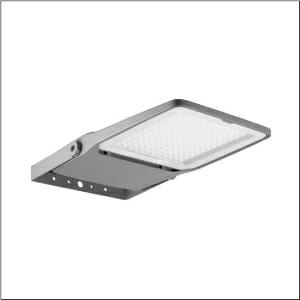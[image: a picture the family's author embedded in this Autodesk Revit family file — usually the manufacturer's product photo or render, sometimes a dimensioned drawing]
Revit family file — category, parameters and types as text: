
# Revit family: floodlight_fl_20_midi___rs17_5xa7682e3b2ac_f562
name_source: partatom
category: Lighting Fixtures
units: mm (PartAtom-declared; Revit-internal decimal feet)

## family parameters
Cut with Voids When Loaded = No
Host = Face
Light Source = No
Part Type = Normal
Room Calculation Point = No
Round Connector Dimension = Use Diameter
Shared = No

## types (1)
- --- (1 x LED 5000K / CRI = 70 (unbekannt), 29600 lm, 5000K)
    Apparent Load = 208 VA
    CIE Flux Codes = 79 92 99 100 100
    Color Rendering = 70
    Color Temperature = 5000K
    Default Elevation = 1800 mm
    Description = Floodlight FL 20 midi, floodlight, primary light control with lens, of plastic, primary optical cover: protective disc, of toughened safety glass, transparent, light distribution: RS17, light emission: direct distribution, primary light characteristic: rotationally symmetric, installation type: surface-mounted, LED, High Power LED, rated luminous flux: 29.600lm, luminous efficacy: 142lm/W, light colour: 750, colour temperature: 5000K, control gear: ECG Plus, control: flexible luminous flux parameterisation, time-dependent luminous flux control, digital communication interface, power reduction, overheat protection, electronic power reduction, with terminal, 5-pole, max. 2.5mm², mains connection: 220..240V, AC, 50/60Hz, rated input power: 208W, LED unit, of diecast aluminium, powder-coated, Siteco® metallic grey (DB 702S), corrosivity category C5 mid according to DIN EN ISO 12944, incl. 1x M20 cable gland for cable Ø 6.5..12mm, length: 731mm, width: 450mm, height: 76mm, housing frame, of diecast aluminium, powder-coated, Siteco® metallic grey (DB 702S), wall fastening, of steel, powder-coated, Siteco® metallic grey (DB 702S), DALI, protection rating (complete): IP66, insulation class (complete): insulation class II (safety insulation), certification: CE, ENEC, VDE, protection symbol: D, permissible operating ambient temperature: -40..+40°C, permissible operating ambient temperature for outdoor applications: -40..+50°C, standard: DIN EN 12944, packaging unit: 1 piece

Light Distribution: RS17
    Height = 76 mm
    Lamp = 1 x LED 5000K / CRI >= 70 (unbekannt)
    Lamp Light Flux = 29600 lm
    Lamp count = 1
    Length = 731 mm
    Luminous efficacy = 142 lm/W
    Manufacturer = Siteco
    ModVariant = No
    Model = 5XA7682E3B2AC
    Mounting Place = Wall
    Mounting Type = Surface mounted
    Number of Poles = 1
    OnlyDefault = Yes
    Power Factor = 1
    Product Name = Floodlight FL 20 midi | RS17
    Product group = floodlight | wall mounted
    ProductGroupID = 2001
    Protection Class = Protection class II
    Protection Degree = IP 66
    RLX_Detail_Level = 1
    RLX_Emergency_Light_Flux = 0 lm
    RLX_Emergency_Type = 0
    RLX_Emergency_Type_DB = No
    RlxData = <blob elided: 86585 chars, md5=e42d9e7b>
    Socket = socket
    Standby Power = 0 W
    System Light Flux = 29600 lm
    System Power = 208 W
    Type Comments = factory setting: luminous flux: 100 % | dim-lin: 254 | 484 mA
    Type Image = l_1005944.jpg
    URL = http://relux.com
    VarID = @adj_146341
    Voltage = 0 V
    Weight = 0.00 kg
    Width = 450 mm

## geometry (parser evidence)
native form markers: Blend x4, Sweep x11
no freeform markers — native parametric forms only
